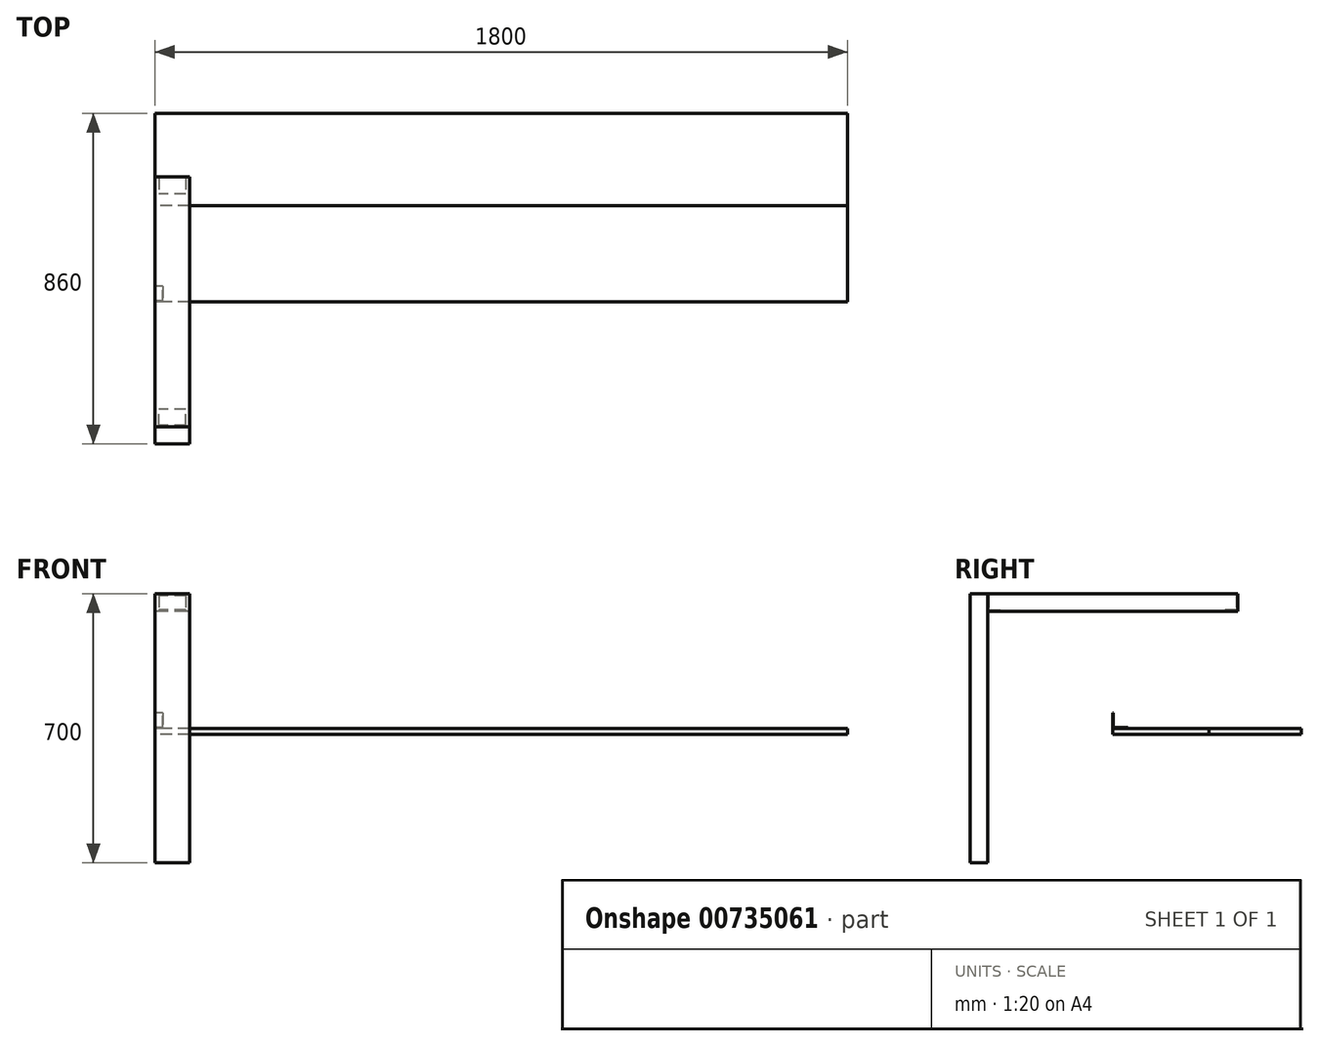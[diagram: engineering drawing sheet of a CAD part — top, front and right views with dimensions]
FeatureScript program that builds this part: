
annotation { "Feature Type Name" : "Feature", "Feature Type Description" : "" }
export const myFeature = defineFeature(function(context is Context, id is Id, definition is map)
    precondition{}
    {
        {
            var Q0;
            Q0=qCreatedBy(makeId("Right.planeOp"),FACE);
            var sketch = newSketch(context, id + "F0", { "sketchPlane" : qUnion([Q0])});
            skLineSegment(sketch, "E0.bottom", {"start": v(-370, 350) * mm, "end": v(370, 350) * mm});
            skLineSegment(sketch, "E0.top", {"start": v(-370, -350) * mm, "end": v(370, -350) * mm});
            skLineSegment(sketch, "E0.left", {"start": v(-370, 350) * mm, "end": v(-370, -350) * mm});
            skLineSegment(sketch, "E0.right", {"start": v(370, 350) * mm, "end": v(370, -350) * mm});
            skPoint(sketch, "E0.middle", {"position": v(0, 0) * mm});
            skLineSegment(sketch, "E1.0", {"start": v(-325, 305) * mm, "end": v(325, 305) * mm});
            skLineSegment(sketch, "E1.1", {"start": v(-325, 305) * mm, "end": v(-325, -305) * mm});
            skLineSegment(sketch, "E1.2", {"start": v(-325, -305) * mm, "end": v(325, -305) * mm});
            skLineSegment(sketch, "E1.3", {"start": v(325, 305) * mm, "end": v(325, -305) * mm});
            skLineSegment(sketch, "E2", {"start": v(-325, 305) * mm, "end": v(-325, 350) * mm});
            skLineSegment(sketch, "E3", {"start": v(-325, -305) * mm, "end": v(-325, -350) * mm});
            skLineSegment(sketch, "E4", {"start": v(325, 305) * mm, "end": v(325, 350) * mm});
            skLineSegment(sketch, "E5", {"start": v(325, -305) * mm, "end": v(325, -350) * mm});
            skSolve(sketch);
        }
        {
            var Q0;
            {var subQ0=sQuery(id+"F0.wireOp",EDGE,"E0.left");Q0=makeQuery(id+"F0.imprint","IMPRINT",FACE,{"disambiguationData":[TD([[makeQuery(id+"F0.imprint","IMPRINT",EDGE,{"derivedFrom":subQ0}),1.0]])]});}
            extrude(context, id + "F1", {"entities" : qUnion([Q0]), "depth" : 90 * mm, "offsetDistance" : 25 * mm});
        }
        {
            var Q0;
            Q0=makeQuery(id+"F0.imprint","IMPRINT",FACE,{"disambiguationData":[TD([[makeQuery(id+"F0.imprint","IMPRINT",EDGE,{"derivedFrom":sQuery(id+"F0.wireOp",EDGE,"E1.0")}),1.0]])]});
            var Q1;
            Q1=makeQuery(id+"F1.opExtrude","CAP_FACE",FACE,{"disambiguationData":[OSD([sQuery(id+"F0.wireOp",EDGE,"E0.bottom"),sQuery(id+"F0.wireOp",EDGE,"E0.top"),sQuery(id+"F0.wireOp",EDGE,"E0.left"),sQuery(id+"F0.wireOp",EDGE,"E1.1"),sQuery(id+"F0.wireOp",EDGE,"E2"),sQuery(id+"F0.wireOp",EDGE,"E3")])],"isStart":false});
            extrude(context, id + "F2", {"entities" : qUnion([Q0]), "endBound" : BoundingType.UP_TO_SURFACE, "depth" : 25 * mm, "endBoundEntityFace" : qUnion([Q1]), "offsetDistance" : 25 * mm});
        }
        {
            var Q0;
            Q0=makeQuery(id+"F2.opExtrude","SWEPT_FACE",FACE,{"disambiguationData":[OSD([sQuery(id+"F0.wireOp",EDGE,"E1.0")])]});
            var sketch = newSketch(context, id + "F3", { "sketchPlane" : qUnion([Q0])});
            skLineSegment(sketch, "E6.bottom", {"start": v(80, 325) * mm, "end": v(10, 325) * mm});
            skLineSegment(sketch, "E6.top", {"start": v(80, 322) * mm, "end": v(10, 322) * mm});
            skLineSegment(sketch, "E6.left", {"start": v(80, 325) * mm, "end": v(80, 322) * mm});
            skLineSegment(sketch, "E6.right", {"start": v(10, 325) * mm, "end": v(10, 322) * mm});
            skLineSegment(sketch, "E7.MirrorCS", {"start": v(10, -325) * mm, "end": v(10, -322) * mm});
            skLineSegment(sketch, "E8.MirrorCS", {"start": v(80, -322) * mm, "end": v(10, -322) * mm});
            skLineSegment(sketch, "E9.MirrorCS", {"start": v(80, -325) * mm, "end": v(10, -325) * mm});
            skLineSegment(sketch, "E10.MirrorCS", {"start": v(80, -325) * mm, "end": v(80, -322) * mm});
            skSolve(sketch);
        }
        {
            var Q0;
            Q0=makeQuery(id+"F3.imprint","IMPRINT",FACE,{"disambiguationData":[TD([[makeQuery(id+"F3.imprint","IMPRINT",EDGE,{"derivedFrom":sQuery(id+"F3.wireOp",EDGE,"E6.bottom")}),1.0]])]});
            var Q1;
            Q1=makeQuery(id+"F3.imprint","IMPRINT",FACE,{"disambiguationData":[TD([[makeQuery(id+"F3.imprint","IMPRINT",EDGE,{"derivedFrom":sQuery(id+"F3.wireOp",EDGE,"E7.MirrorCS")}),-1.0]])]});
            extrude(context, id + "F4", {"entities" : qUnion([Q0, Q1]), "operationType" : NewBodyOperationType.REMOVE, "oppositeDirection" : true, "depth" : 40 * mm, "offsetDistance" : 25 * mm});
        }
        {
            var Q0;
            Q0=makeQuery(id+"F2.opExtrude","SWEPT_FACE",FACE,{"disambiguationData":[OSD([sQuery(id+"F0.wireOp",EDGE,"E1.0")])]});
            var sketch = newSketch(context, id + "F5", { "sketchPlane" : qUnion([Q0])});
            skLineSegment(sketch, "E11.bottom", {"start": v(80, 322) * mm, "end": v(10, 322) * mm});
            skLineSegment(sketch, "E11.top", {"start": v(80, 280) * mm, "end": v(10, 280) * mm});
            skLineSegment(sketch, "E11.left", {"start": v(80, 322) * mm, "end": v(80, 280) * mm});
            skLineSegment(sketch, "E11.right", {"start": v(10, 322) * mm, "end": v(10, 280) * mm});
            skLineSegment(sketch, "E12.MirrorCS", {"start": v(10, -322) * mm, "end": v(10, -280) * mm});
            skLineSegment(sketch, "E13.MirrorCS", {"start": v(80, -280) * mm, "end": v(10, -280) * mm});
            skLineSegment(sketch, "E14.MirrorCS", {"start": v(80, -322) * mm, "end": v(80, -280) * mm});
            skLineSegment(sketch, "E15.MirrorCS", {"start": v(80, -322) * mm, "end": v(10, -322) * mm});
            skSolve(sketch);
        }
        {
            var Q0;
            Q0=makeQuery(id+"F5.imprint","IMPRINT",FACE,{"disambiguationData":[TD([[makeQuery(id+"F5.imprint","IMPRINT",EDGE,{"derivedFrom":sQuery(id+"F5.wireOp",EDGE,"E11.bottom")}),1.0]])]});
            var Q1;
            Q1=makeQuery(id+"F5.imprint","IMPRINT",FACE,{"disambiguationData":[TD([[makeQuery(id+"F5.imprint","IMPRINT",EDGE,{"derivedFrom":sQuery(id+"F5.wireOp",EDGE,"E12.MirrorCS")}),-1.0]])]});
            extrude(context, id + "F6", {"entities" : qUnion([Q0, Q1]), "operationType" : NewBodyOperationType.REMOVE, "oppositeDirection" : true, "depth" : 3 * mm, "offsetDistance" : 25 * mm});
        }
        {
            var Q0;
            Q0=qCreatedBy(makeId("Right.planeOp"),FACE);
            var sketch = newSketch(context, id + "F7", { "sketchPlane" : qUnion([Q0])});
            skLineSegment(sketch, "E16", {"start": v(0, 40) * mm, "end": v(0, 0) * mm});
            skLineSegment(sketch, "E17", {"start": v(0, 0) * mm, "end": v(40, 0) * mm});
            skLineSegment(sketch, "E18", {"start": v(40, 0) * mm, "end": v(40, 2) * mm});
            skLineSegment(sketch, "E19", {"start": v(40, 2) * mm, "end": v(2, 2) * mm});
            skLineSegment(sketch, "E20", {"start": v(2, 2) * mm, "end": v(2, 40) * mm});
            skLineSegment(sketch, "E21", {"start": v(2, 40) * mm, "end": v(0, 40) * mm});
            skSolve(sketch);
        }
        {
            var Q0;
            Q0=makeQuery(id+"F7.imprint","IMPRINT",FACE,{"disambiguationData":[TD([[makeQuery(id+"F7.imprint","IMPRINT",EDGE,{"derivedFrom":sQuery(id+"F7.wireOp",EDGE,"E16")}),1.0]])]});
            extrude(context, id + "F8", {"entities" : qUnion([Q0]), "depth" : 20 * mm, "offsetDistance" : 25 * mm});
        }
        {
            var Q0;
            Q0=qCreatedBy(makeId("Right.planeOp"),FACE);
            var sketch = newSketch(context, id + "F9", { "sketchPlane" : qUnion([Q0])});
            skLineSegment(sketch, "E22.bottom", {"start": v(0, 0) * mm, "end": v(250, 0) * mm});
            skLineSegment(sketch, "E22.top", {"start": v(0, -16) * mm, "end": v(250, -16) * mm});
            skLineSegment(sketch, "E22.left", {"start": v(0, 0) * mm, "end": v(0, -16) * mm});
            skLineSegment(sketch, "E22.right", {"start": v(250, 0) * mm, "end": v(250, -16) * mm});
            skLineSegment(sketch, "E23.bottom", {"start": v(250, -16) * mm, "end": v(490, -16) * mm});
            skLineSegment(sketch, "E23.top", {"start": v(250, 0) * mm, "end": v(490, 0) * mm});
            skLineSegment(sketch, "E23.left", {"start": v(250, -16) * mm, "end": v(250, 0) * mm});
            skLineSegment(sketch, "E23.right", {"start": v(490, -16) * mm, "end": v(490, 0) * mm});
            skSolve(sketch);
        }
        {
            var Q0;
            Q0=makeQuery(id+"F9.imprint","IMPRINT",FACE,{"disambiguationData":[TD([[makeQuery(id+"F9.imprint","IMPRINT",EDGE,{"derivedFrom":sQuery(id+"F9.wireOp",EDGE,"E22.bottom")}),-1.0]])]});
            extrude(context, id + "F10", {"entities" : qUnion([Q0]), "depth" : 1800 * mm, "offsetDistance" : 25 * mm});
        }
        {
            var Q0;
            Q0=makeQuery(id+"F9.imprint","IMPRINT",FACE,{"disambiguationData":[TD([[makeQuery(id+"F9.imprint","IMPRINT",EDGE,{"derivedFrom":sQuery(id+"F9.wireOp",EDGE,"E23.bottom")}),1.0]])]});
            extrude(context, id + "F11", {"entities" : qUnion([Q0]), "depth" : 1800 * mm, "offsetDistance" : 25 * mm});
        }
    });
